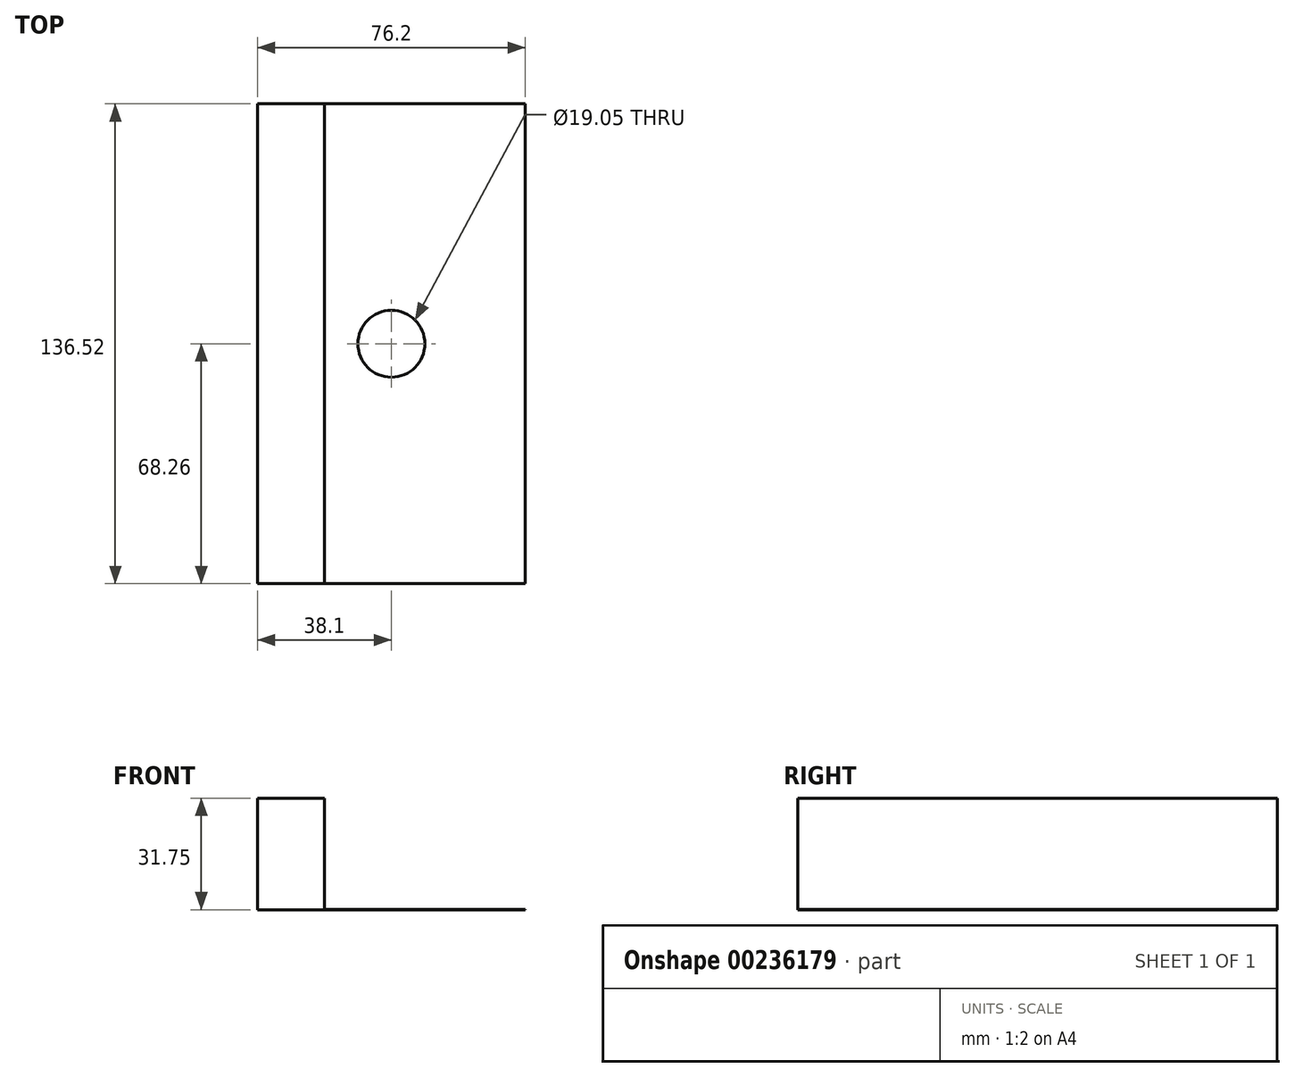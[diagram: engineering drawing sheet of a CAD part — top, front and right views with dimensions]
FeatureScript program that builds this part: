
annotation { "Feature Type Name" : "Feature", "Feature Type Description" : "" }
export const myFeature = defineFeature(function(context is Context, id is Id, definition is map)
    precondition{}
    {
        {
            var Q0;
            Q0=qCreatedBy(makeId("Top.planeOp"),FACE);
            var sketch = newSketch(context, id + "F0", { "sketchPlane" : qUnion([Q0])});
            skLineSegment(sketch, "E0.bottom", {"start": v(-38.1, 68.26) * mm, "end": v(38.1, 68.26) * mm});
            skLineSegment(sketch, "E0.top", {"start": v(-38.1, -68.26) * mm, "end": v(38.1, -68.26) * mm});
            skLineSegment(sketch, "E0.left", {"start": v(-38.1, 68.26) * mm, "end": v(-38.1, -68.26) * mm});
            skLineSegment(sketch, "E0.right", {"start": v(38.1, 68.26) * mm, "end": v(38.1, -68.26) * mm});
            skPoint(sketch, "E0.middle", {"position": v(0, 0) * mm});
            skSolve(sketch);
        }
        {
            var Q0;
            Q0=makeQuery(id+"F0.imprint","IMPRINT",FACE,{"disambiguationData":[TD([[makeQuery(id+"F0.imprint","IMPRINT",EDGE,{"derivedFrom":sQuery(id+"F0.wireOp",EDGE,"E0.bottom")}),-1.0]])]});
            extrude(context, id + "F1", {"entities" : qUnion([Q0]), "depth" : 3 / 101.6 * mm});
        }
        {
            var Q0;
            Q0=makeQuery(id+"F1.opExtrude","SWEPT_FACE",FACE,{"disambiguationData":[OSD([sQuery(id+"F0.wireOp",EDGE,"E0.top")])]});
            var sketch = newSketch(context, id + "F2", { "sketchPlane" : qUnion([Q0])});
            skLineSegment(sketch, "E1", {"start": v(38.1, 0) * mm, "end": v(38.1, 31.75) * mm});
            skLineSegment(sketch, "E2", {"start": v(38.1, 31.75) * mm, "end": v(19.05, 31.75) * mm});
            skLineSegment(sketch, "E3", {"start": v(19.05, 31.75) * mm, "end": v(19.05, 19.05) * mm});
            skLineSegment(sketch, "E4", {"start": v(-38.1, 0) * mm, "end": v(-38.1, 31.75) * mm});
            skLineSegment(sketch, "E5", {"start": v(-38.1, 31.75) * mm, "end": v(-19.05, 31.75) * mm});
            skLineSegment(sketch, "E6", {"start": v(-19.05, 31.75) * mm, "end": v(-19.05, 0) * mm});
            skSolve(sketch);
        }
        {
            var Q0;
            {var subQ3=sQuery(id+"F2.wireOp",EDGE,"E5");Q0=makeQuery(id+"F2.imprint","IMPRINT",FACE,{"disambiguationData":[TD([[makeQuery(id+"F2.imprint","IMPRINT",EDGE,{"derivedFrom":subQ3}),-1.0]])]});}
            var Q1;
            {var subQ3=sQuery(id+"F2.wireOp",EDGE,"E2");Q1=makeQuery(id+"F2.imprint","IMPRINT",FACE,{"disambiguationData":[TD([[makeQuery(id+"F2.imprint","IMPRINT",EDGE,{"derivedFrom":subQ3}),1.0]])]});}
            extrude(context, id + "F3", {"entities" : qUnion([Q0, Q1]), "operationType" : NewBodyOperationType.ADD, "oppositeDirection" : true, "depth" : 136.53 * mm});
        }
        {
            var Q0;
            Q0=qCreatedBy(makeId("Top.planeOp"),FACE);
            var sketch = newSketch(context, id + "F4", { "sketchPlane" : qUnion([Q0])});
            skLineSegment(sketch, "E7", {"start": v(0, 0) * mm, "end": v(0, 68.26) * mm});
            skCircle(sketch, "E8", {"center": v(0, 0) * mm, "radius": 9.53 * mm});
            skSolve(sketch);
        }
        {
            var Q0;
            Q0=sQuery(id+"F4.wireOp",VERTEX,"E7.start");
            var Q1;
            Q1=makeQuery(id+"F1.opExtrude","SWEPT_BODY",BODY,{"disambiguationData":[OSD([sQuery(id+"F0.wireOp",EDGE,"E0.bottom"),sQuery(id+"F0.wireOp",EDGE,"E0.top"),sQuery(id+"F0.wireOp",EDGE,"E0.left"),sQuery(id+"F0.wireOp",EDGE,"E0.right")])]});
            hole(context, id + "F5", {"style" : HoleStyle.C_BORE, "endStyle" : HoleEndStyle.THROUGH, "oppositeDirection" : true, "holeDiameter" : 6.35 * mm, "cBoreDiameter" : 19.05 * mm, "cBoreDepth" : 12.7 * mm, "locations" : qUnion([Q0]), "scope" : qUnion([Q1]), "isTappedThrough" : true});
        }
    });
